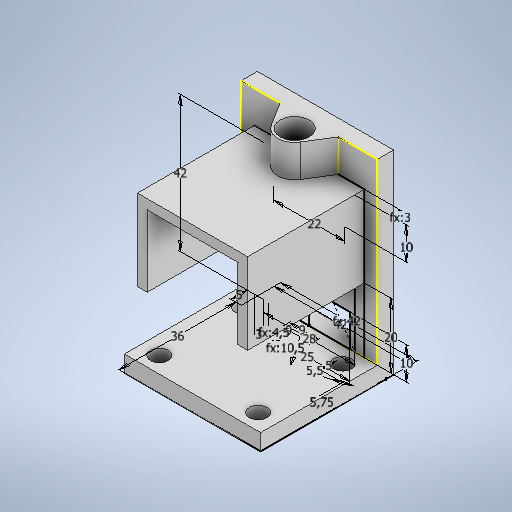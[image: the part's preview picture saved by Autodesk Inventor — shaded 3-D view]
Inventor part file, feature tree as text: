
AUTODESK INVENTOR PART (.ipt)
format: ipt  version: 2025 (Build 290162000, 162)  size: 344,576 bytes
history: native  units: mm
features: extrude x6, sketch x2, other x1, projected_geometry x1
ambient origin geometry x8: Origin, YZ Plane, XZ Plane, XY Plane, X Axis, Y Axis, Z Axis, Center Point
bodies: Body1 (feature_tree)
feature tree (10):
  other  "Bryła1"
  sketch  "Szkic1"
  extrude  "Wyciągnięcie proste1"  Depth=5.5mm
  extrude  "Wyciągnięcie proste2"  Depth=5.75mm
  extrude  "Wyciągnięcie proste3"  Depth=5.0mm
  extrude  "Wyciągnięcie proste4"  Depth=5.0mm
  sketch  "Szkic3"
  extrude  "Wyciągnięcie proste5"  Depth=42.0mm
  extrude  "Wyciągnięcie proste6"  Depth=4.5mm
  projected_geometry  "Pętla rzutowana1"
